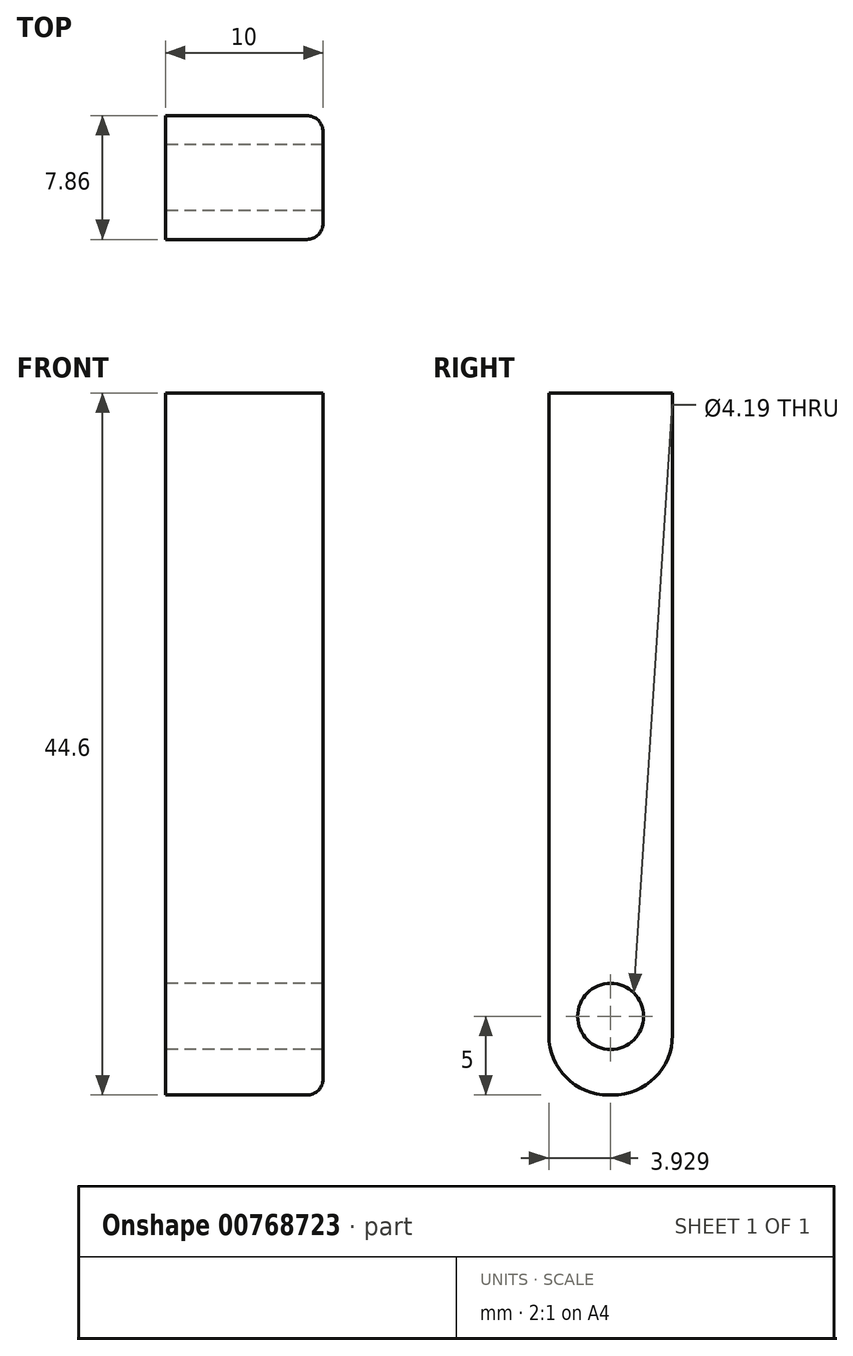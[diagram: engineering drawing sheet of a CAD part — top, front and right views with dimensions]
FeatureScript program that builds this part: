
annotation { "Feature Type Name" : "Feature", "Feature Type Description" : "" }
export const myFeature = defineFeature(function(context is Context, id is Id, definition is map)
    precondition{}
    {
        {
            var Q0;
            Q0=qCreatedBy(makeId("Right.planeOp"),FACE);
            var sketch = newSketch(context, id + "F0", { "sketchPlane" : qUnion([Q0])});
            skLineSegment(sketch, "E0.bottom", {"start": v(-3.8, 0) * mm, "end": v(-4.05, 0) * mm});
            skLineSegment(sketch, "E0.top", {"start": v(0, 44.6) * mm, "end": v(-7.86, 44.6) * mm});
            skLineSegment(sketch, "E0.left", {"start": v(0, 3.81) * mm, "end": v(0, 44.6) * mm});
            skLineSegment(sketch, "E0.right", {"start": v(-7.86, 3.81) * mm, "end": v(-7.86, 44.6) * mm});
            skLineSegment(sketch, "E1", {"start": v(-7.86, 10) * mm, "end": v(0, 10) * mm, "construction": true});
            skLineSegment(sketch, "E2", {"start": v(-7.86, 10) * mm, "end": v(0, 0) * mm, "construction": true});
            skLineSegment(sketch, "E3", {"start": v(0, 10) * mm, "end": v(-7.86, 0) * mm, "construction": true});
            skCircle(sketch, "E4", {"center": v(-3.93, 5) * mm, "radius": 2.1 * mm});
            skPoint(sketch, "E5.visualSharp", {"position": v(0, 0) * mm});
            skArc(sketch, "E5.filletArc", {"start": v(-3.8, 0) * mm, "mid": v(-1.12, 1.12) * mm, "end": v(0, 3.81) * mm});
            skPoint(sketch, "E6.visualSharp", {"position": v(-7.86, 0) * mm});
            skArc(sketch, "E6.filletArc", {"start": v(-7.86, 3.8) * mm, "mid": v(-6.75, 1.12) * mm, "end": v(-4.05, 0) * mm});
            skSolve(sketch);
        }
        {
            var Q0;
            Q0=makeQuery(id+"F0.imprint","IMPRINT",FACE,{"disambiguationData":[TD([[makeQuery(id+"F0.imprint","IMPRINT",EDGE,{"derivedFrom":sQuery(id+"F0.wireOp",EDGE,"E0.bottom")}),-1.0]])]});
            extrude(context, id + "F1", {"entities" : qUnion([Q0]), "depth" : 10 * mm, "offsetDistance" : 25.4 * mm});
        }
        {
            var Q0;
            Q0=makeQuery(id+"F1.opExtrude","CAP_EDGE",EDGE,{"disambiguationData":[OSD([sQuery(id+"F0.wireOp",EDGE,"E0.left")])],"isStart":false});
            fillet(context, id + "F2", {"entities" : qUnion([Q0]), "radius" : 1.02 * mm, "tangentPropagation" : true, "allowEdgeOverflow" : false});
        }
    });
